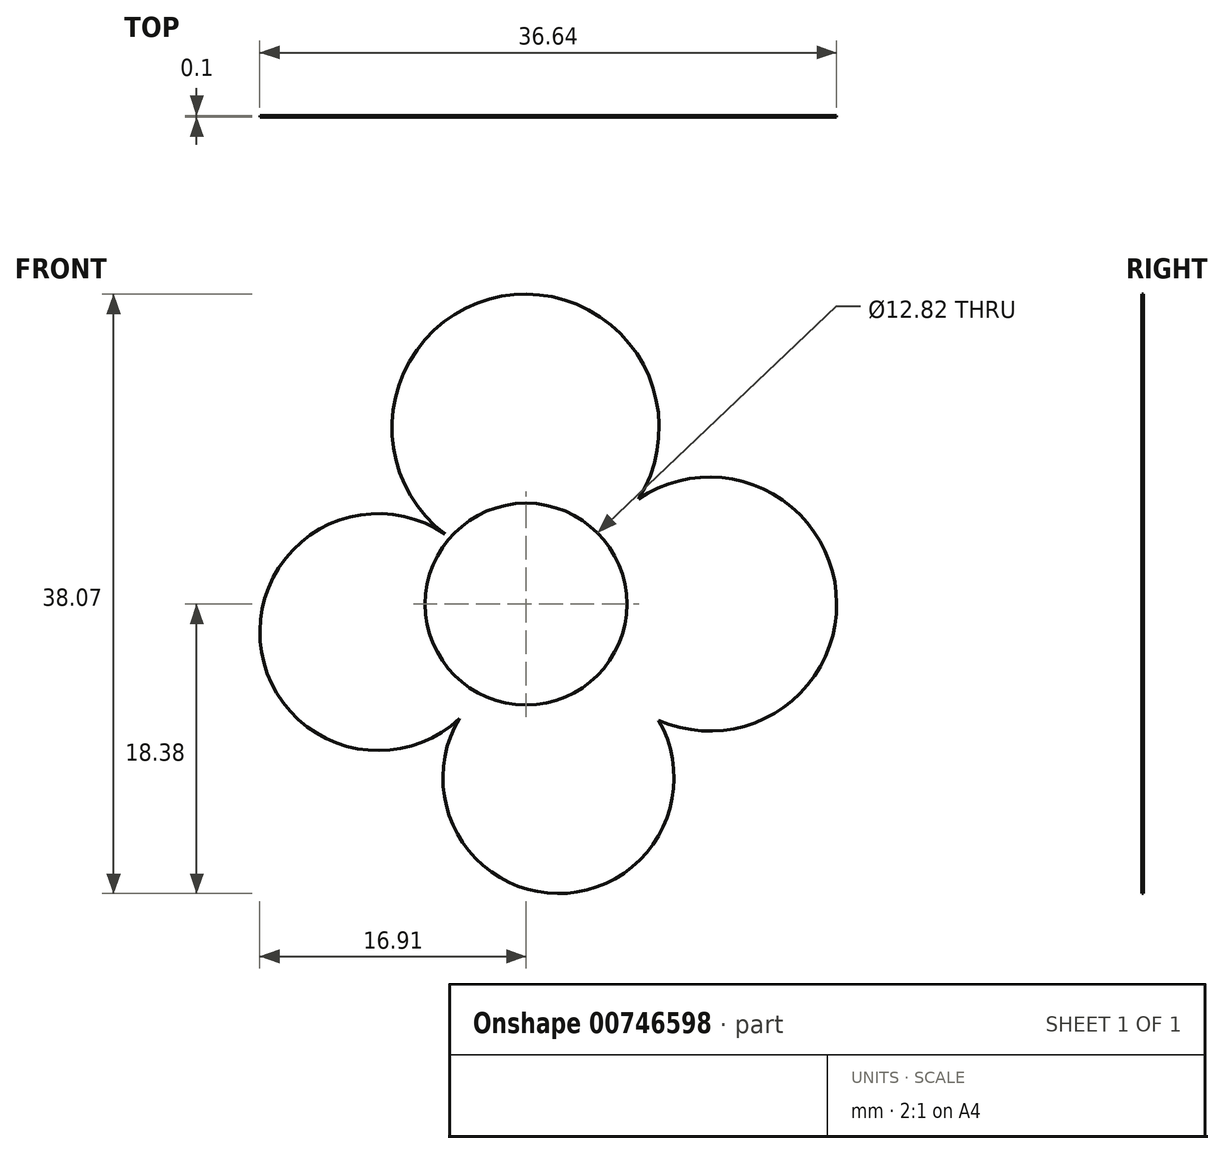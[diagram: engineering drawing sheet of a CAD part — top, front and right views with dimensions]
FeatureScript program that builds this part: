
annotation { "Feature Type Name" : "Feature", "Feature Type Description" : "" }
export const myFeature = defineFeature(function(context is Context, id is Id, definition is map)
    precondition{}
    {
        {
            var Q0;
            Q0=qCreatedBy(makeId("Front.planeOp"),FACE);
            var sketch = newSketch(context, id + "F0", { "sketchPlane" : qUnion([Q0])});
            skCircle(sketch, "E0", {"center": v(0, 0) * mm, "radius": 6.4 * mm});
            skArc(sketch, "E1", {"start": v(4.8, 4.24) * mm, "mid": v(-0.05, 19.69) * mm, "end": v(-4.83, 4.21) * mm});
            skArc(sketch, "E2", {"start": v(4.8, -4.24) * mm, "mid": v(19.73, 0) * mm, "end": v(4.8, 4.24) * mm});
            skArc(sketch, "E3", {"start": v(-2.95, -5.69) * mm, "mid": v(3.4, -18.26) * mm, "end": v(4.8, -4.24) * mm});
            skArc(sketch, "E4", {"start": v(-4.83, 4.21) * mm, "mid": v(-16.78, -3.18) * mm, "end": v(-2.95, -5.69) * mm});
            skSolve(sketch);
        }
        {
            var Q0;
            Q0 = qSketchRegion(id + "F0", true);
            extrude(context, id + "F1", {"entities" : qUnion([Q0]), "depth" : .10 * mm, "offsetDistance" : 25 * mm});
        }
    });
